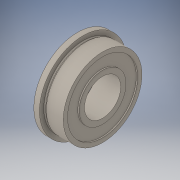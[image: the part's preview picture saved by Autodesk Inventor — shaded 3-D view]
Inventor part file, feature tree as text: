
AUTODESK INVENTOR PART (.ipt)
format: ipt  version: 2019.3 (Build 233278000, 278)  size: 174,080 bytes
history: native  units: in
note: dims shown in document units (in); Inventor stores cm internally (conversion verified against a paired STEP export)
features: revolve x1
ambient origin geometry x8: Origin, YZ Plane, XZ Plane, XY Plane, X Axis, Y Axis, Z Axis, Center Point
bodies: Solid1 (feature_tree)
feature tree (1):
  revolve  "Revolve1"  [1 undecoded]
note: 1 required parameter value undecoded (feature->parameter linkage not recoverable at this tier; creation-order binding heuristic only, values carry confidence <= 0.55)
